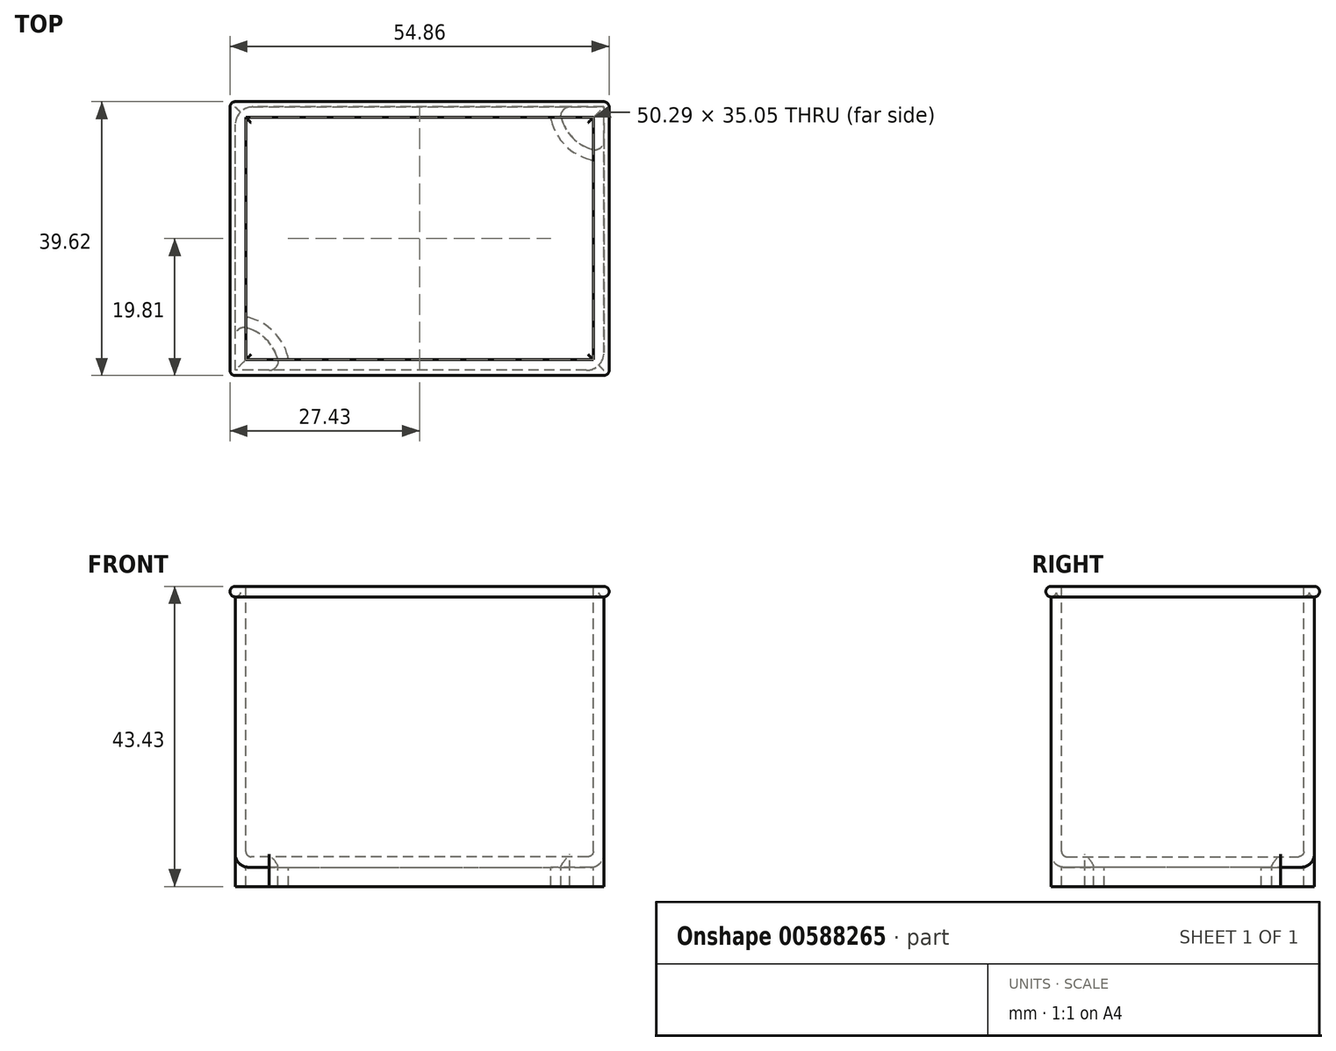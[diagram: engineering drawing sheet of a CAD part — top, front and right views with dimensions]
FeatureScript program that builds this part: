
annotation { "Feature Type Name" : "Feature", "Feature Type Description" : "" }
export const myFeature = defineFeature(function(context is Context, id is Id, definition is map)
    precondition{}
    {
        {
            var Q0;
            Q0=qCreatedBy(makeId("Front.planeOp"),FACE);
            var sketch = newSketch(context, id + "F0", { "sketchPlane" : qUnion([Q0])});
            skLineSegment(sketch, "E0.bottom", {"start": v(26.67, -20.32) * mm, "end": v(-26.67, -20.32) * mm});
            skLineSegment(sketch, "E0.top", {"start": v(26.67, 20.32) * mm, "end": v(-26.67, 20.32) * mm});
            skLineSegment(sketch, "E0.left", {"start": v(26.67, -20.32) * mm, "end": v(26.67, 20.32) * mm});
            skLineSegment(sketch, "E0.right", {"start": v(-26.67, -20.32) * mm, "end": v(-26.67, 20.32) * mm});
            skPoint(sketch, "E0.middle", {"position": v(0, 0) * mm});
            skSolve(sketch);
        }
        {
            var Q0;
            Q0=makeQuery(id+"F0.imprint","IMPRINT",FACE,{"disambiguationData":[TD([[makeQuery(id+"F0.imprint","IMPRINT",EDGE,{"derivedFrom":sQuery(id+"F0.wireOp",EDGE,"E0.bottom")}),-1.0]])]});
            extrude(context, id + "F1", {"entities" : qUnion([Q0]), "endBound" : BoundingType.SYMMETRIC, "depth" : 38.1 * mm});
        }
        {
            var Q0;
            Q0=makeQuery(id+"F1.opExtrude","SWEPT_FACE",FACE,{"disambiguationData":[OSD([sQuery(id+"F0.wireOp",EDGE,"E0.top")])]});
            shell(context, id + "F2", {"entities" : qUnion([Q0]), "thickness" : 1.52 * mm});
        }
        {
            var Q0;
            Q0=makeQuery(id+"F1.opExtrude","CAP_FACE",FACE,{"disambiguationData":[OSD([sQuery(id+"F0.wireOp",EDGE,"E0.bottom"),sQuery(id+"F0.wireOp",EDGE,"E0.top"),sQuery(id+"F0.wireOp",EDGE,"E0.left"),sQuery(id+"F0.wireOp",EDGE,"E0.right")])],"isStart":false});
            var sketch = newSketch(context, id + "F3", { "sketchPlane" : qUnion([Q0])});
            skArc(sketch, "E1", {"start": v(-26.67, 20.32) * mm, "mid": v(-27.43, 19.56) * mm, "end": v(-26.67, 18.8) * mm});
            skSolve(sketch);
        }
        {
            var Q0;
            {var subQ0=sQuery(id+"F3.wireOp",EDGE,"E1");Q0=makeQuery(id+"F3.imprint","IMPRINT",FACE,{"disambiguationData":[TD([[makeQuery(id+"F3.imprint","IMPRINT",EDGE,{"derivedFrom":subQ0}),1.0]])]});}
            var Q1;
            Q1=makeQuery(id+"F1.opExtrude","SWEPT_EDGE",EDGE,{"disambiguationData":[OSD([sQuery(id+"F0.wireOp",EDGE,"E0.top"),sQuery(id+"F0.wireOp",EDGE,"E0.right")])]});
            var Q2;
            Q2=makeQuery(id+"F1.opExtrude","CAP_EDGE",EDGE,{"disambiguationData":[OSD([sQuery(id+"F0.wireOp",EDGE,"E0.top")])],"isStart":true});
            var Q3;
            Q3=makeQuery(id+"F1.opExtrude","SWEPT_EDGE",EDGE,{"disambiguationData":[OSD([sQuery(id+"F0.wireOp",EDGE,"E0.top"),sQuery(id+"F0.wireOp",EDGE,"E0.left")])]});
            var Q4;
            Q4=makeQuery(id+"F1.opExtrude","CAP_EDGE",EDGE,{"disambiguationData":[OSD([sQuery(id+"F0.wireOp",EDGE,"E0.top")])],"isStart":false});
            sweep(context, id + "F4", {"operationType" : NewBodyOperationType.ADD, "profiles" : qUnion([Q0]), "path" : qUnion([Q1, Q2, Q3, Q4])});
        }
        {
            var Q0;
            Q0=makeQuery(id+"F1.opExtrude","SWEPT_FACE",FACE,{"disambiguationData":[OSD([sQuery(id+"F0.wireOp",EDGE,"E0.bottom")])]});
            var sketch = newSketch(context, id + "F5", { "sketchPlane" : qUnion([Q0])});
            skLineSegment(sketch, "E2.bottom", {"start": v(26.67, 19.05) * mm, "end": v(21.75, 19.05) * mm});
            skLineSegment(sketch, "E2.left", {"start": v(26.67, 19.05) * mm, "end": v(26.67, 14.13) * mm});
            skPoint(sketch, "E3.newPointA", {"position": v(20.32, 19.05) * mm});
            skArc(sketch, "E4", {"start": v(20.52, 17.46) * mm, "mid": v(22.18, 14.56) * mm, "end": v(25.08, 12.9) * mm});
            skArc(sketch, "E5.filletArc", {"start": v(21.75, 19.05) * mm, "mid": v(20.75, 18.56) * mm, "end": v(20.52, 17.46) * mm});
            skPoint(sketch, "E6.visualSharp", {"position": v(26.67, 12.7) * mm});
            skArc(sketch, "E6.filletArc", {"start": v(25.08, 12.9) * mm, "mid": v(26.18, 13.13) * mm, "end": v(26.67, 14.13) * mm});
            skArc(sketch, "E7.MirrorCS", {"start": v(-21.75, 19.05) * mm, "mid": v(-20.75, 18.56) * mm, "end": v(-20.52, 17.46) * mm});
            skArc(sketch, "E8.MirrorCS", {"start": v(-20.52, 17.46) * mm, "mid": v(-22.18, 14.56) * mm, "end": v(-25.08, 12.9) * mm});
            skArc(sketch, "E9.MirrorCS", {"start": v(-25.08, 12.9) * mm, "mid": v(-26.18, 13.13) * mm, "end": v(-26.67, 14.13) * mm});
            skLineSegment(sketch, "E10.MirrorCS", {"start": v(-26.67, 19.05) * mm, "end": v(-26.67, 14.13) * mm});
            skLineSegment(sketch, "E11.MirrorCS", {"start": v(-26.67, 19.05) * mm, "end": v(-21.75, 19.05) * mm});
            skArc(sketch, "E12.MirrorCS", {"start": v(-20.52, -17.46) * mm, "mid": v(-22.18, -14.56) * mm, "end": v(-25.08, -12.9) * mm});
            skArc(sketch, "E13.MirrorCS", {"start": v(-21.75, -19.05) * mm, "mid": v(-20.75, -18.56) * mm, "end": v(-20.52, -17.46) * mm});
            skLineSegment(sketch, "E14.MirrorCS", {"start": v(-26.67, -19.05) * mm, "end": v(-21.75, -19.05) * mm});
            skLineSegment(sketch, "E15.MirrorCS", {"start": v(-26.67, -19.05) * mm, "end": v(-26.67, -14.13) * mm});
            skArc(sketch, "E16.MirrorCS", {"start": v(-25.08, -12.9) * mm, "mid": v(-26.18, -13.13) * mm, "end": v(-26.67, -14.13) * mm});
            skArc(sketch, "E17.MirrorCS", {"start": v(21.75, -19.05) * mm, "mid": v(20.75, -18.56) * mm, "end": v(20.52, -17.46) * mm});
            skArc(sketch, "E18.MirrorCS", {"start": v(20.52, -17.46) * mm, "mid": v(22.18, -14.56) * mm, "end": v(25.08, -12.9) * mm});
            skArc(sketch, "E19.MirrorCS", {"start": v(25.08, -12.9) * mm, "mid": v(26.18, -13.13) * mm, "end": v(26.67, -14.13) * mm});
            skLineSegment(sketch, "E20.MirrorCS", {"start": v(26.67, -19.05) * mm, "end": v(26.67, -14.13) * mm});
            skLineSegment(sketch, "E21.MirrorCS", {"start": v(26.67, -19.05) * mm, "end": v(21.75, -19.05) * mm});
            skSolve(sketch);
        }
        {
            var Q0;
            Q0=makeQuery(id+"F5.imprint","IMPRINT",FACE,{"disambiguationData":[TD([[makeQuery(id+"F5.imprint","IMPRINT",EDGE,{"derivedFrom":sQuery(id+"F5.wireOp",EDGE,"E2.bottom")}),1.0]])]});
            var Q1;
            Q1=makeQuery(id+"F5.imprint","IMPRINT",FACE,{"disambiguationData":[TD([[makeQuery(id+"F5.imprint","IMPRINT",EDGE,{"derivedFrom":sQuery(id+"F5.wireOp",EDGE,"E8.MirrorCS")}),-1.0]])]});
            var Q2;
            Q2=makeQuery(id+"F5.imprint","IMPRINT",FACE,{"disambiguationData":[TD([[makeQuery(id+"F5.imprint","IMPRINT",EDGE,{"derivedFrom":sQuery(id+"F5.wireOp",EDGE,"E12.MirrorCS")}),1.0]])]});
            var Q3;
            Q3=makeQuery(id+"F5.imprint","IMPRINT",FACE,{"disambiguationData":[TD([[makeQuery(id+"F5.imprint","IMPRINT",EDGE,{"derivedFrom":sQuery(id+"F5.wireOp",EDGE,"E17.MirrorCS")}),-1.0]])]});
            extrude(context, id + "F6", {"entities" : qUnion([Q0, Q1, Q2, Q3]), "operationType" : NewBodyOperationType.ADD, "depth" : 2.8 * mm});
        }
        {
            var Q0;
            Q0=makeQuery(id+"F6.opExtrude","CAP_FACE",FACE,{"disambiguationData":[OSD([sQuery(id+"F5.wireOp",EDGE,"E2.bottom"),sQuery(id+"F5.wireOp",EDGE,"E2.left"),sQuery(id+"F5.wireOp",EDGE,"E4"),sQuery(id+"F5.wireOp",EDGE,"E5.filletArc"),sQuery(id+"F5.wireOp",EDGE,"E6.filletArc")])],"isStart":false});
            var Q1;
            Q1=makeQuery(id+"F6.opExtrude","CAP_FACE",FACE,{"disambiguationData":[OSD([sQuery(id+"F5.wireOp",EDGE,"E8.MirrorCS"),sQuery(id+"F5.wireOp",EDGE,"E9.MirrorCS"),sQuery(id+"F5.wireOp",EDGE,"E10.MirrorCS"),sQuery(id+"F5.wireOp",EDGE,"E7.MirrorCS"),sQuery(id+"F5.wireOp",EDGE,"E11.MirrorCS")])],"isStart":false});
            var Q2;
            Q2=makeQuery(id+"F6.opExtrude","CAP_FACE",FACE,{"disambiguationData":[OSD([sQuery(id+"F5.wireOp",EDGE,"E12.MirrorCS"),sQuery(id+"F5.wireOp",EDGE,"E13.MirrorCS"),sQuery(id+"F5.wireOp",EDGE,"E14.MirrorCS"),sQuery(id+"F5.wireOp",EDGE,"E15.MirrorCS"),sQuery(id+"F5.wireOp",EDGE,"E16.MirrorCS")])],"isStart":false});
            var Q3;
            Q3=makeQuery(id+"F6.opExtrude","CAP_FACE",FACE,{"disambiguationData":[OSD([sQuery(id+"F5.wireOp",EDGE,"E17.MirrorCS"),sQuery(id+"F5.wireOp",EDGE,"E18.MirrorCS"),sQuery(id+"F5.wireOp",EDGE,"E19.MirrorCS"),sQuery(id+"F5.wireOp",EDGE,"E20.MirrorCS"),sQuery(id+"F5.wireOp",EDGE,"E21.MirrorCS")])],"isStart":false});
            shell(context, id + "F7", {"entities" : qUnion([Q0, Q1, Q2, Q3]), "thickness" : 1.52 * mm});
        }
        {
            var Q0;
            Q0=makeQuery(id+"F2.opShell","OFFSET_FACE",FACE,{"disambiguationData":[OSD([sQuery(id+"F0.wireOp",EDGE,"E0.bottom")])]});
            fillet(context, id + "F8", {"entities" : qUnion([Q0]), "radius" : 0.76 * mm, "tangentPropagation" : true, "allowEdgeOverflow" : false});
        }
        {
            var Q0;
            Q0=makeQuery(id+"F1.opExtrude","SWEPT_EDGE",EDGE,{"disambiguationData":[OSD([sQuery(id+"F0.wireOp",EDGE,"E0.bottom"),sQuery(id+"F0.wireOp",EDGE,"E0.right")])]});
            var Q1;
            Q1=makeQuery(id+"F1.opExtrude","CAP_EDGE",EDGE,{"disambiguationData":[OSD([sQuery(id+"F0.wireOp",EDGE,"E0.bottom")])],"isStart":false});
            var Q2;
            Q2=makeQuery(id+"F1.opExtrude","SWEPT_EDGE",EDGE,{"disambiguationData":[OSD([sQuery(id+"F0.wireOp",EDGE,"E0.bottom"),sQuery(id+"F0.wireOp",EDGE,"E0.left")])]});
            var Q3;
            Q3=makeQuery(id+"F1.opExtrude","CAP_EDGE",EDGE,{"disambiguationData":[OSD([sQuery(id+"F0.wireOp",EDGE,"E0.bottom")])],"isStart":true});
            fillet(context, id + "F9", {"entities" : qUnion([Q0, Q1, Q2, Q3]), "radius" : 1.9 * mm, "tangentPropagation" : true, "allowEdgeOverflow" : false});
        }
        {
            var Q0;
            Q0=makeQuery(id+"F4.opSweep","MID_CAP_EDGE",EDGE,{"disambiguationData":[OSD([sQuery(id+"F0.wireOp",EDGE,"E0.top"),sQuery(id+"F0.wireOp",EDGE,"E0.left"),sQuery(id+"F3.wireOp",EDGE,"E1")])],"capPos":3.0});
            var Q1;
            Q1=makeQuery(id+"F4.opSweep","MID_CAP_EDGE",EDGE,{"disambiguationData":[OSD([sQuery(id+"F0.wireOp",EDGE,"E0.top"),sQuery(id+"F0.wireOp",EDGE,"E0.left"),sQuery(id+"F3.wireOp",EDGE,"E1")])],"capPos":2.0});
            var Q2;
            Q2=makeQuery(id+"F4.opSweep","MID_CAP_EDGE",EDGE,{"disambiguationData":[OSD([sQuery(id+"F0.wireOp",EDGE,"E0.top"),sQuery(id+"F0.wireOp",EDGE,"E0.right"),sQuery(id+"F3.wireOp",EDGE,"E1")])],"capPos":1.0});
            var Q3;
            Q3=makeQuery(id+"F4.opSweep","CAP_EDGE",EDGE,{"disambiguationData":[OSD([sQuery(id+"F0.wireOp",EDGE,"E0.top"),sQuery(id+"F0.wireOp",EDGE,"E0.right"),sQuery(id+"F3.wireOp",EDGE,"E1")])],"isStart":true});
            fillet(context, id + "F10", {"entities" : qUnion([Q0, Q1, Q2, Q3]), "radius" : 0.76 * mm, "tangentPropagation" : true, "allowEdgeOverflow" : false});
        }
        {
            var Q0;
            Q0=makeQuery(id+"F6.boolean.opBoolean","MERGE",EDGE,{"derivedFrom":[makeQuery(id+"F1.opExtrude","CAP_EDGE",EDGE,{"disambiguationData":[OSD([sQuery(id+"F0.wireOp",EDGE,"E0.left")])],"isStart":false}),makeQuery(id+"F6.opExtrude","SWEPT_EDGE",EDGE,{"disambiguationData":[OSD([sQuery(id+"F5.wireOp",EDGE,"E2.bottom"),sQuery(id+"F5.wireOp",EDGE,"E2.left")])]})]});
            var Q1;
            Q1=makeQuery(id+"F6.boolean.opBoolean","MERGE",EDGE,{"derivedFrom":[makeQuery(id+"F1.opExtrude","CAP_EDGE",EDGE,{"disambiguationData":[OSD([sQuery(id+"F0.wireOp",EDGE,"E0.left")])],"isStart":true}),makeQuery(id+"F6.opExtrude","SWEPT_EDGE",EDGE,{"disambiguationData":[OSD([sQuery(id+"F5.wireOp",EDGE,"E20.MirrorCS"),sQuery(id+"F5.wireOp",EDGE,"E21.MirrorCS")])]})]});
            var Q2;
            Q2=makeQuery(id+"F6.boolean.opBoolean","MERGE",EDGE,{"derivedFrom":[makeQuery(id+"F1.opExtrude","CAP_EDGE",EDGE,{"disambiguationData":[OSD([sQuery(id+"F0.wireOp",EDGE,"E0.right")])],"isStart":false}),makeQuery(id+"F6.opExtrude","SWEPT_EDGE",EDGE,{"disambiguationData":[OSD([sQuery(id+"F5.wireOp",EDGE,"E10.MirrorCS"),sQuery(id+"F5.wireOp",EDGE,"E11.MirrorCS")])]})]});
            var Q3;
            Q3=makeQuery(id+"F6.boolean.opBoolean","MERGE",EDGE,{"derivedFrom":[makeQuery(id+"F1.opExtrude","CAP_EDGE",EDGE,{"disambiguationData":[OSD([sQuery(id+"F0.wireOp",EDGE,"E0.right")])],"isStart":true}),makeQuery(id+"F6.opExtrude","SWEPT_EDGE",EDGE,{"disambiguationData":[OSD([sQuery(id+"F5.wireOp",EDGE,"E14.MirrorCS"),sQuery(id+"F5.wireOp",EDGE,"E15.MirrorCS")])]})]});
            fillet(context, id + "F11", {"entities" : qUnion([Q0, Q1, Q2, Q3]), "radius" : 2.54 * mm, "tangentPropagation" : true, "allowEdgeOverflow" : false});
        }
    });
